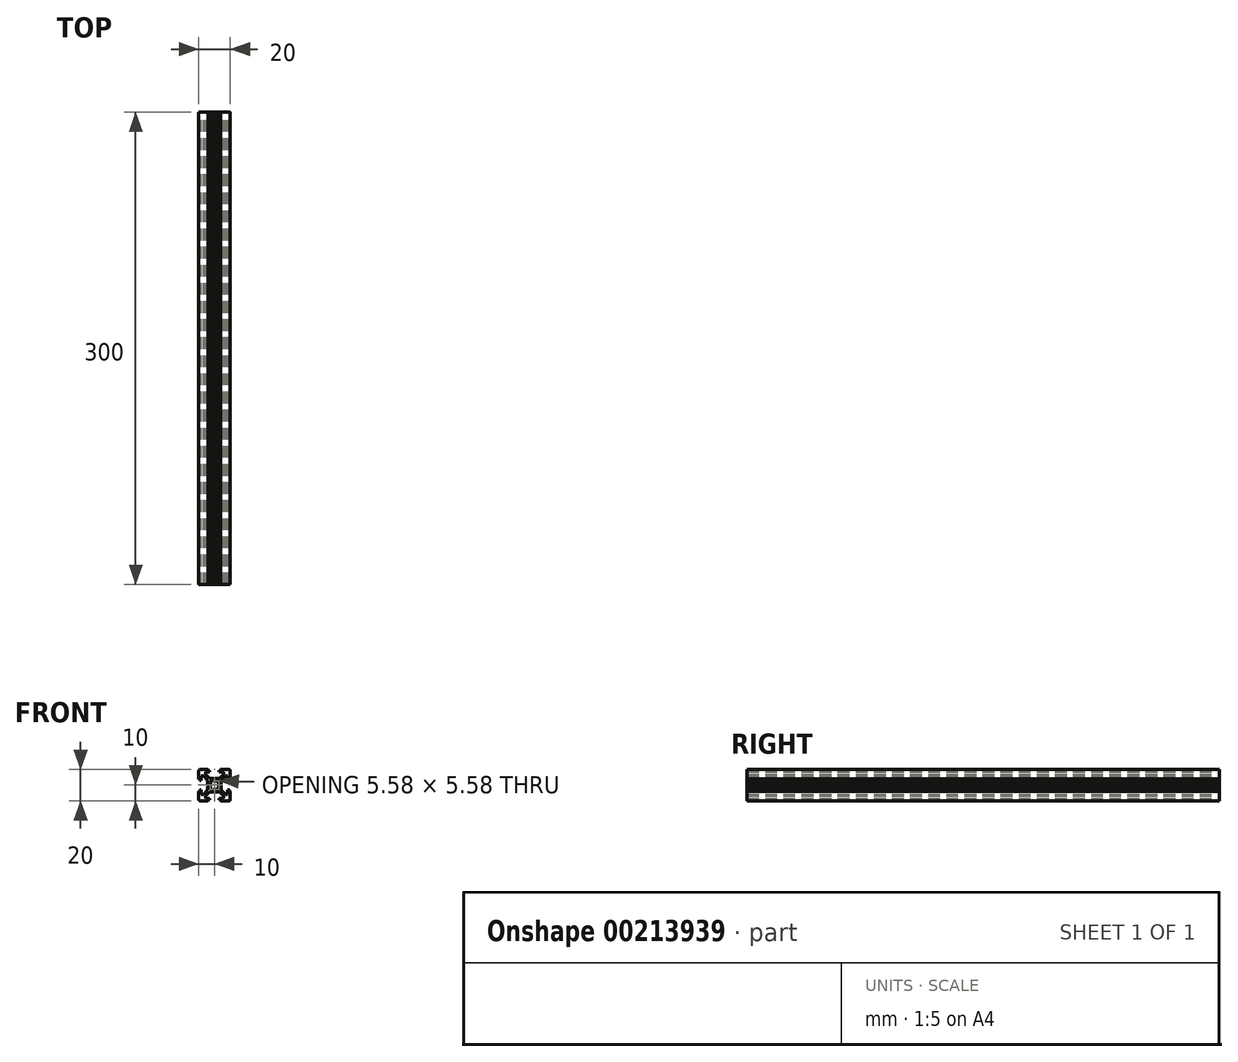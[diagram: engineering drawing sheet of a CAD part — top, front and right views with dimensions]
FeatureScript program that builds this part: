
annotation { "Feature Type Name" : "Feature", "Feature Type Description" : "" }
export const myFeature = defineFeature(function(context is Context, id is Id, definition is map)
    precondition{}
    {
        {
            var Q0;
            Q0=qCreatedBy(makeId("Front.planeOp"),FACE);
            var sketch = newSketch(context, id + "F0", { "sketchPlane" : qUnion([Q0])});
            skArc(sketch, "E0", {"start": v(-2.43, 1.3) * mm, "mid": v(-2.67, 0.67) * mm, "end": v(-2.75, 0) * mm});
            skPoint(sketch, "E1.visualSharp", {"position": v(-10, 10) * mm});
            skArc(sketch, "E1.filletArc", {"start": v(-9, 10) * mm, "mid": v(-9.7, 9.7) * mm, "end": v(-10, 9) * mm});
            skLineSegment(sketch, "E2", {"start": v(-3.85, 0) * mm, "end": v(0, 0) * mm, "construction": true});
            skLineSegment(sketch, "E3", {"start": v(0, 3.85) * mm, "end": v(0, 0) * mm, "construction": true});
            skLineSegment(sketch, "E4.0", {"start": v(-9.5, 3) * mm, "end": v(-8.4, 3) * mm});
            skLineSegment(sketch, "E5.0", {"start": v(-3, 9.5) * mm, "end": v(-3, 8.4) * mm});
            skLineSegment(sketch, "E6.trimOffspring", {"start": v(-10, 4) * mm, "end": v(-10, 9) * mm});
            skLineSegment(sketch, "E7.trimOffspring", {"start": v(-4, 10) * mm, "end": v(-9, 10) * mm});
            skLineSegment(sketch, "E8.0", {"start": v(-3, 8.4) * mm, "end": v(-5.8, 8.4) * mm});
            skLineSegment(sketch, "E8.1", {"start": v(-8.4, 3) * mm, "end": v(-8.4, 5.8) * mm});
            skLineSegment(sketch, "E9", {"start": v(-8.4, 8.4) * mm, "end": v(0, 0) * mm, "construction": true});
            skLineSegment(sketch, "E10.0", {"start": v(-5.8, 6.93) * mm, "end": v(-3.12, 4.25) * mm});
            skLineSegment(sketch, "E11.0", {"start": v(-6.93, 5.8) * mm, "end": v(-4.25, 3.12) * mm});
            skArc(sketch, "E12.trimOffspring", {"start": v(-1.66, 2.79) * mm, "mid": v(-2.3, 2.3) * mm, "end": v(-2.79, 1.66) * mm});
            skLineSegment(sketch, "E13.top", {"start": v(-10, 4) * mm, "end": v(-9.5, 4) * mm});
            skLineSegment(sketch, "E13.right", {"start": v(-9.5, 3) * mm, "end": v(-9.5, 4) * mm});
            skLineSegment(sketch, "E14.top", {"start": v(-3, 9.5) * mm, "end": v(-4, 9.5) * mm});
            skLineSegment(sketch, "E14.right", {"start": v(-4, 10) * mm, "end": v(-4, 9.5) * mm});
            skLineSegment(sketch, "E15.bottom", {"start": v(-3.12, 4.25) * mm, "end": v(-0.75, 4.25) * mm});
            skLineSegment(sketch, "E15.left", {"start": v(-4.25, 3.12) * mm, "end": v(-4.25, 0.75) * mm});
            skLineSegment(sketch, "E16", {"start": v(-8.4, 5.8) * mm, "end": v(-6.93, 5.8) * mm});
            skLineSegment(sketch, "E17", {"start": v(-5.8, 8.4) * mm, "end": v(-5.8, 6.93) * mm});
            skPoint(sketch, "E18.orphan", {"position": v(-4.25, 4.25) * mm});
            skLineSegment(sketch, "E19.trimOffspring", {"start": v(-2.79, 1.66) * mm, "end": v(-2.43, 1.3) * mm});
            skLineSegment(sketch, "E20.trimOffspring", {"start": v(-1.66, 2.79) * mm, "end": v(-1.3, 2.43) * mm});
            skLineSegment(sketch, "E21", {"start": v(-4.25, 0.75) * mm, "end": v(-3.85, 0) * mm});
            skPoint(sketch, "E22.orphan", {"position": v(-4.25, 0) * mm});
            skLineSegment(sketch, "E23", {"start": v(0, 3.85) * mm, "end": v(-0.75, 4.25) * mm});
            skPoint(sketch, "E24.orphan", {"position": v(0, 4.25) * mm});
            skArc(sketch, "E25.trimOffspring", {"start": v(0, 2.75) * mm, "mid": v(-0.67, 2.67) * mm, "end": v(-1.3, 2.43) * mm});
            skLineSegment(sketch, "E26", {"start": v(0, 2.75) * mm, "end": v(0, 3.85) * mm});
            skLineSegment(sketch, "E27", {"start": v(-3.85, 0) * mm, "end": v(-2.75, 0) * mm});
            skSolve(sketch);
        }
        {
            var Q0;
            Q0 = qSketchRegion(id + "F0", true);
            extrude(context, id + "F1", {"entities" : qUnion([Q0]), "depth" : 300 * mm});
        }
        {
            var Q0;
            Q0=qCreatedBy(makeId("Top.planeOp"),FACE);
            var sketch = newSketch(context, id + "F2", { "sketchPlane" : qUnion([Q0])});
            skLineSegment(sketch, "E28", {"start": v(0, 0) * mm, "end": v(0, -300) * mm, "construction": true});
            skSolve(sketch);
        }
        {
            var Q0;
            Q0=makeQuery(id+"F1.opExtrude","SWEPT_BODY",BODY,{"disambiguationData":[OSD([sQuery(id+"F0.wireOp",EDGE,"E0"),sQuery(id+"F0.wireOp",EDGE,"E1.filletArc"),sQuery(id+"F0.wireOp",EDGE,"E4.0"),sQuery(id+"F0.wireOp",EDGE,"E5.0"),sQuery(id+"F0.wireOp",EDGE,"E6.trimOffspring"),sQuery(id+"F0.wireOp",EDGE,"E7.trimOffspring"),sQuery(id+"F0.wireOp",EDGE,"E8.0"),sQuery(id+"F0.wireOp",EDGE,"E8.1"),sQuery(id+"F0.wireOp",EDGE,"E10.0"),sQuery(id+"F0.wireOp",EDGE,"E11.0"),sQuery(id+"F0.wireOp",EDGE,"E12.trimOffspring"),sQuery(id+"F0.wireOp",EDGE,"E13.top"),sQuery(id+"F0.wireOp",EDGE,"E13.right"),sQuery(id+"F0.wireOp",EDGE,"E14.top"),sQuery(id+"F0.wireOp",EDGE,"E14.right"),sQuery(id+"F0.wireOp",EDGE,"E15.bottom"),sQuery(id+"F0.wireOp",EDGE,"E15.left"),sQuery(id+"F0.wireOp",EDGE,"E16"),sQuery(id+"F0.wireOp",EDGE,"E17"),sQuery(id+"F0.wireOp",EDGE,"E19.trimOffspring"),sQuery(id+"F0.wireOp",EDGE,"E20.trimOffspring"),sQuery(id+"F0.wireOp",EDGE,"E21"),sQuery(id+"F0.wireOp",EDGE,"E23"),sQuery(id+"F0.wireOp",EDGE,"E25.trimOffspring"),sQuery(id+"F0.wireOp",EDGE,"E26"),sQuery(id+"F0.wireOp",EDGE,"E27")])]});
            var Q1;
            Q1=sQuery(id+"F2.wireOp",EDGE,"E28");
            circularPattern(context, id + "F3", {"operationType" : NewBodyOperationType.ADD, "entities" : qUnion([Q0]), "axis" : qUnion([Q1]), "angle" : 360 * degree, "instanceCount" : 4, "equalSpace" : true});
        }
    });
